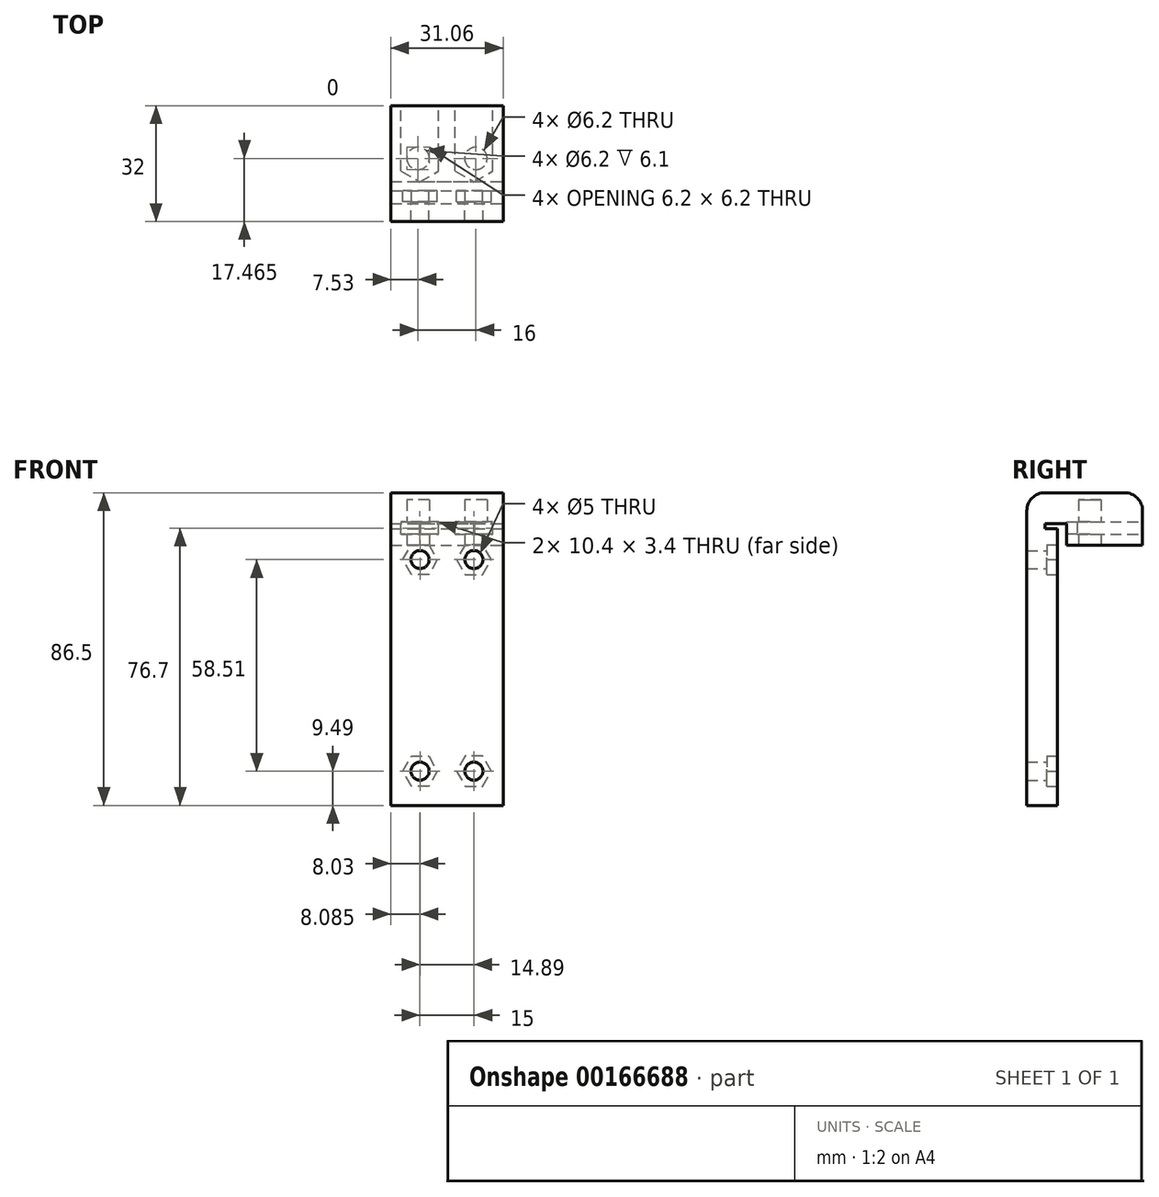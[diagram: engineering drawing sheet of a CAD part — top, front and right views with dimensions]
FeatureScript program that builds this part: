
annotation { "Feature Type Name" : "Feature", "Feature Type Description" : "" }
export const myFeature = defineFeature(function(context is Context, id is Id, definition is map)
    precondition{}
    {
        {
            var Q0;
            Q0=qCreatedBy(makeId("Right.planeOp"),FACE);
            var sketch = newSketch(context, id + "F0", { "sketchPlane" : qUnion([Q0])});
            skLineSegment(sketch, "E0", {"start": v(-5, -75) * mm, "end": v(-5, 11.5) * mm});
            skLineSegment(sketch, "E1", {"start": v(-5, 11.5) * mm, "end": v(27, 11.5) * mm});
            skLineSegment(sketch, "E2", {"start": v(27, 11.5) * mm, "end": v(27, -3) * mm});
            skLineSegment(sketch, "E3", {"start": v(27, -3) * mm, "end": v(6, -3) * mm});
            skLineSegment(sketch, "E4", {"start": v(6, -3) * mm, "end": v(6, 3) * mm});
            skLineSegment(sketch, "E5", {"start": v(6, 3) * mm, "end": v(0, 3) * mm});
            skLineSegment(sketch, "E6", {"start": v(0, 3) * mm, "end": v(0, -75) * mm});
            skLineSegment(sketch, "E7", {"start": v(0, -75) * mm, "end": v(-5, -75) * mm});
            skLineSegment(sketch, "E8", {"start": v(0, 1.5) * mm, "end": v(3.5, 1.5) * mm});
            skLineSegment(sketch, "E9", {"start": v(3.5, 1.5) * mm, "end": v(3.5, -75) * mm});
            skLineSegment(sketch, "E10", {"start": v(3.5, -75) * mm, "end": v(0, -75) * mm});
            skLineSegment(sketch, "E11", {"start": v(0, -75) * mm, "end": v(0, 1.5) * mm});
            skSolve(sketch);
        }
        {
            var Q0;
            Q0=qSketchRegion(id+"F0",true);
            extrude(context, id + "F1", {"entities" : qUnion([Q0]), "depth" : 31.05 * mm, "symmetric" : true});
        }
        {
            var Q0;
            Q0=makeQuery(id+"F1.opExtrude","SWEPT_EDGE",EDGE,{"disambiguationData":[OSD([sQuery(id+"F0.wireOp",EDGE,"E0"),sQuery(id+"F0.wireOp",EDGE,"E1")])]});
            fillet(context, id + "F2", {"entities" : qUnion([Q0]), "radius" : 5 * mm, "tangentPropagation" : true, "allowEdgeOverflow" : false});
        }
        {
            var Q0;
            Q0=makeQuery(id+"F1.opExtrude","SWEPT_EDGE",EDGE,{"disambiguationData":[OSD([sQuery(id+"F0.wireOp",EDGE,"E1"),sQuery(id+"F0.wireOp",EDGE,"E2")])]});
            fillet(context, id + "F3", {"entities" : qUnion([Q0]), "radius" : 5 * mm, "tangentPropagation" : true, "allowEdgeOverflow" : false});
        }
        {
            var Q0;
            Q0=qCreatedBy(makeId("Front.planeOp"),FACE);
            var sketch = newSketch(context, id + "F4", { "sketchPlane" : qUnion([Q0])});
            skCircle(sketch, "E12", {"center": v(-7.45, -7) * mm, "radius": 2.5 * mm});
            skCircle(sketch, "E13", {"center": v(-7.44, -65.5) * mm, "radius": 2.5 * mm});
            skSolve(sketch);
        }
        {
            var Q0;
            Q0=qCreatedBy(makeId("Front.planeOp"),FACE);
            var sketch = newSketch(context, id + "F5", { "sketchPlane" : qUnion([Q0])});
            skCircle(sketch, "E14.cCircle", {"center": v(-7.45, -7) * mm, "radius": 4.15 * mm, "construction": true});
            skLineSegment(sketch, "E14.0", {"start": v(-9.84, -11.15) * mm, "end": v(-12.24, -7) * mm});
            skLineSegment(sketch, "E14.1", {"start": v(-12.24, -7) * mm, "end": v(-9.84, -2.85) * mm});
            skLineSegment(sketch, "E14.2", {"start": v(-9.84, -2.85) * mm, "end": v(-5.05, -2.85) * mm});
            skLineSegment(sketch, "E14.3", {"start": v(-5.05, -2.85) * mm, "end": v(-2.65, -7) * mm});
            skLineSegment(sketch, "E14.4", {"start": v(-2.65, -7) * mm, "end": v(-5.05, -11.15) * mm});
            skLineSegment(sketch, "E14.5", {"start": v(-5.05, -11.15) * mm, "end": v(-9.84, -11.15) * mm});
            skPoint(sketch, "E14.0.midPoint", {"position": v(-11.04, -9.07) * mm});
            skCircle(sketch, "E15.cCircle", {"center": v(-7.44, -65.5) * mm, "radius": 4.15 * mm, "construction": true});
            skLineSegment(sketch, "E15.0", {"start": v(-9.84, -69.66) * mm, "end": v(-12.24, -65.51) * mm});
            skLineSegment(sketch, "E15.1", {"start": v(-12.24, -65.5) * mm, "end": v(-9.84, -61.36) * mm});
            skLineSegment(sketch, "E15.2", {"start": v(-9.84, -61.36) * mm, "end": v(-5.05, -61.36) * mm});
            skLineSegment(sketch, "E15.3", {"start": v(-5.05, -61.36) * mm, "end": v(-2.65, -65.51) * mm});
            skLineSegment(sketch, "E15.4", {"start": v(-2.65, -65.51) * mm, "end": v(-5.05, -69.66) * mm});
            skLineSegment(sketch, "E15.5", {"start": v(-5.05, -69.66) * mm, "end": v(-9.84, -69.66) * mm});
            skPoint(sketch, "E15.0.midPoint", {"position": v(-11.04, -67.58) * mm});
            skSolve(sketch);
        }
        {
            var Q0;
            Q0=makeQuery(id+"F1.opExtrude","SWEPT_BODY",BODY,{"disambiguationData":[OSD([sQuery(id+"F0.wireOp",EDGE,"E0"),sQuery(id+"F0.wireOp",EDGE,"E1"),sQuery(id+"F0.wireOp",EDGE,"E2"),sQuery(id+"F0.wireOp",EDGE,"E3"),sQuery(id+"F0.wireOp",EDGE,"E4"),sQuery(id+"F0.wireOp",EDGE,"E5"),sQuery(id+"F0.wireOp",EDGE,"E6"),sQuery(id+"F0.wireOp",EDGE,"E7"),sQuery(id+"F0.wireOp",EDGE,"E8"),sQuery(id+"F0.wireOp",EDGE,"E9"),sQuery(id+"F0.wireOp",EDGE,"E10")])]});
            var Q1;
            Q1=makeQuery(id+"F1.opExtrude","SWEPT_FACE",FACE,{"disambiguationData":[OSD([sQuery(id+"F0.wireOp",EDGE,"E0")])]});
            transform(context, id + "F6", {"entities" : qUnion([Q0]), "transformType" : TransformType.TRANSLATION_DISTANCE, "transformDirection" : qUnion([Q1]), "distance" : 3.5 * mm, "makeCopy" : false});
        }
        {
            var Q0;
            Q0 = qSketchRegion(id + "F4", true);
            extrude(context, id + "F7", {"entities" : qUnion([Q0]), "operationType" : NewBodyOperationType.REMOVE, "endBound" : BoundingType.THROUGH_ALL, "depth" : 25 * mm});
        }
        {
            var Q0;
            Q0 = qSketchRegion(id + "F5", true);
            extrude(context, id + "F8", {"entities" : qUnion([Q0]), "operationType" : NewBodyOperationType.REMOVE, "depth" : 3 * mm});
        }
        {
            var Q0;
            Q0=makeQuery(id+"F1.opExtrude","SWEPT_FACE",FACE,{"disambiguationData":[OSD([sQuery(id+"F0.wireOp",EDGE,"E3")])]});
            var sketch = newSketch(context, id + "F9", { "sketchPlane" : qUnion([Q0])});
            skCircle(sketch, "E16", {"center": v(-8, -8.96) * mm, "radius": 3.1 * mm});
            skCircle(sketch, "E17", {"center": v(8, -8.96) * mm, "radius": 3.1 * mm});
            skSolve(sketch);
        }
        {
            var Q0;
            Q0 = qSketchRegion(id + "F9", true);
            extrude(context, id + "F10", {"entities" : qUnion([Q0]), "operationType" : NewBodyOperationType.REMOVE, "oppositeDirection" : true, "depth" : 12.5 * mm});
        }
        {
            var Q0;
            Q0=qCreatedBy(makeId("Top.planeOp"),FACE);
            var sketch = newSketch(context, id + "F11", { "sketchPlane" : qUnion([Q0])});
            skCircle(sketch, "E18.cCircle", {"center": v(-7.5, 8.46) * mm, "radius": 5.2 * mm, "construction": true});
            skLineSegment(sketch, "E18.0", {"start": v(-2.3, 5.46) * mm, "end": v(-7.5, 2.46) * mm});
            skLineSegment(sketch, "E18.1", {"start": v(-7.5, 2.46) * mm, "end": v(-12.7, 5.46) * mm});
            skLineSegment(sketch, "E18.2", {"start": v(-12.7, 5.46) * mm, "end": v(-12.7, 11.47) * mm});
            skLineSegment(sketch, "E18.3", {"start": v(-12.7, 11.47) * mm, "end": v(-7.5, 14.47) * mm});
            skLineSegment(sketch, "E18.4", {"start": v(-7.5, 14.47) * mm, "end": v(-2.3, 11.47) * mm});
            skLineSegment(sketch, "E18.5", {"start": v(-2.3, 11.47) * mm, "end": v(-2.3, 5.46) * mm});
            skPoint(sketch, "E18.0.midPoint", {"position": v(-4.9, 3.96) * mm});
            skCircle(sketch, "E19.cCircle", {"center": v(7.5, 8.46) * mm, "radius": 5.2 * mm, "construction": true});
            skLineSegment(sketch, "E19.0", {"start": v(12.7, 5.46) * mm, "end": v(7.5, 2.46) * mm});
            skLineSegment(sketch, "E19.1", {"start": v(7.5, 2.46) * mm, "end": v(2.3, 5.46) * mm});
            skLineSegment(sketch, "E19.2", {"start": v(2.3, 5.46) * mm, "end": v(2.3, 11.47) * mm});
            skLineSegment(sketch, "E19.3", {"start": v(2.3, 11.47) * mm, "end": v(7.5, 14.47) * mm});
            skLineSegment(sketch, "E19.4", {"start": v(7.5, 14.47) * mm, "end": v(12.7, 11.47) * mm});
            skLineSegment(sketch, "E19.5", {"start": v(12.7, 11.47) * mm, "end": v(12.7, 5.46) * mm});
            skPoint(sketch, "E19.0.midPoint", {"position": v(10.1, 3.96) * mm});
            skPoint(sketch, "E20.oppositeSnap0", {"position": v(12.7, 8.47) * mm});
            skPoint(sketch, "E21.oppositeSnap0", {"position": v(-2.3, 8.46) * mm});
            skLineSegment(sketch, "E21.bottom", {"start": v(-12.7, 5.46) * mm, "end": v(-2.3, 5.46) * mm});
            skLineSegment(sketch, "E21.top", {"start": v(-12.7, 28.6) * mm, "end": v(-2.3, 28.6) * mm});
            skLineSegment(sketch, "E21.left", {"start": v(-12.7, 5.46) * mm, "end": v(-12.7, 28.6) * mm});
            skLineSegment(sketch, "E21.right", {"start": v(-2.3, 5.46) * mm, "end": v(-2.3, 28.6) * mm});
            skLineSegment(sketch, "E22.bottom", {"start": v(2.3, 5.46) * mm, "end": v(12.7, 5.46) * mm});
            skLineSegment(sketch, "E22.top", {"start": v(2.3, 28.6) * mm, "end": v(12.7, 28.6) * mm});
            skLineSegment(sketch, "E22.left", {"start": v(2.3, 5.46) * mm, "end": v(2.3, 28.6) * mm});
            skLineSegment(sketch, "E22.right", {"start": v(12.7, 5.46) * mm, "end": v(12.7, 28.6) * mm});
            skSolve(sketch);
        }
        {
            var Q0;
            Q0 = qSketchRegion(id + "F11", true);
            extrude(context, id + "F12", {"entities" : qUnion([Q0]), "operationType" : NewBodyOperationType.REMOVE, "depth" : 3.4 * mm});
        }
        {
            var Q0;
            Q0=makeQuery(id+"F1.opExtrude","SWEPT_BODY",BODY,{"disambiguationData":[OSD([sQuery(id+"F0.wireOp",EDGE,"E0"),sQuery(id+"F0.wireOp",EDGE,"E1"),sQuery(id+"F0.wireOp",EDGE,"E2"),sQuery(id+"F0.wireOp",EDGE,"E3"),sQuery(id+"F0.wireOp",EDGE,"E4"),sQuery(id+"F0.wireOp",EDGE,"E5"),sQuery(id+"F0.wireOp",EDGE,"E6"),sQuery(id+"F0.wireOp",EDGE,"E7"),sQuery(id+"F0.wireOp",EDGE,"E8"),sQuery(id+"F0.wireOp",EDGE,"E9"),sQuery(id+"F0.wireOp",EDGE,"E10")])]});
            var Q1;
            Q1=qCreatedBy(makeId("Right.planeOp"),FACE);
            mirror(context, id + "F13", {"entities" : qUnion([Q0]), "mirrorPlane" : qUnion([Q1])});
        }
    });
